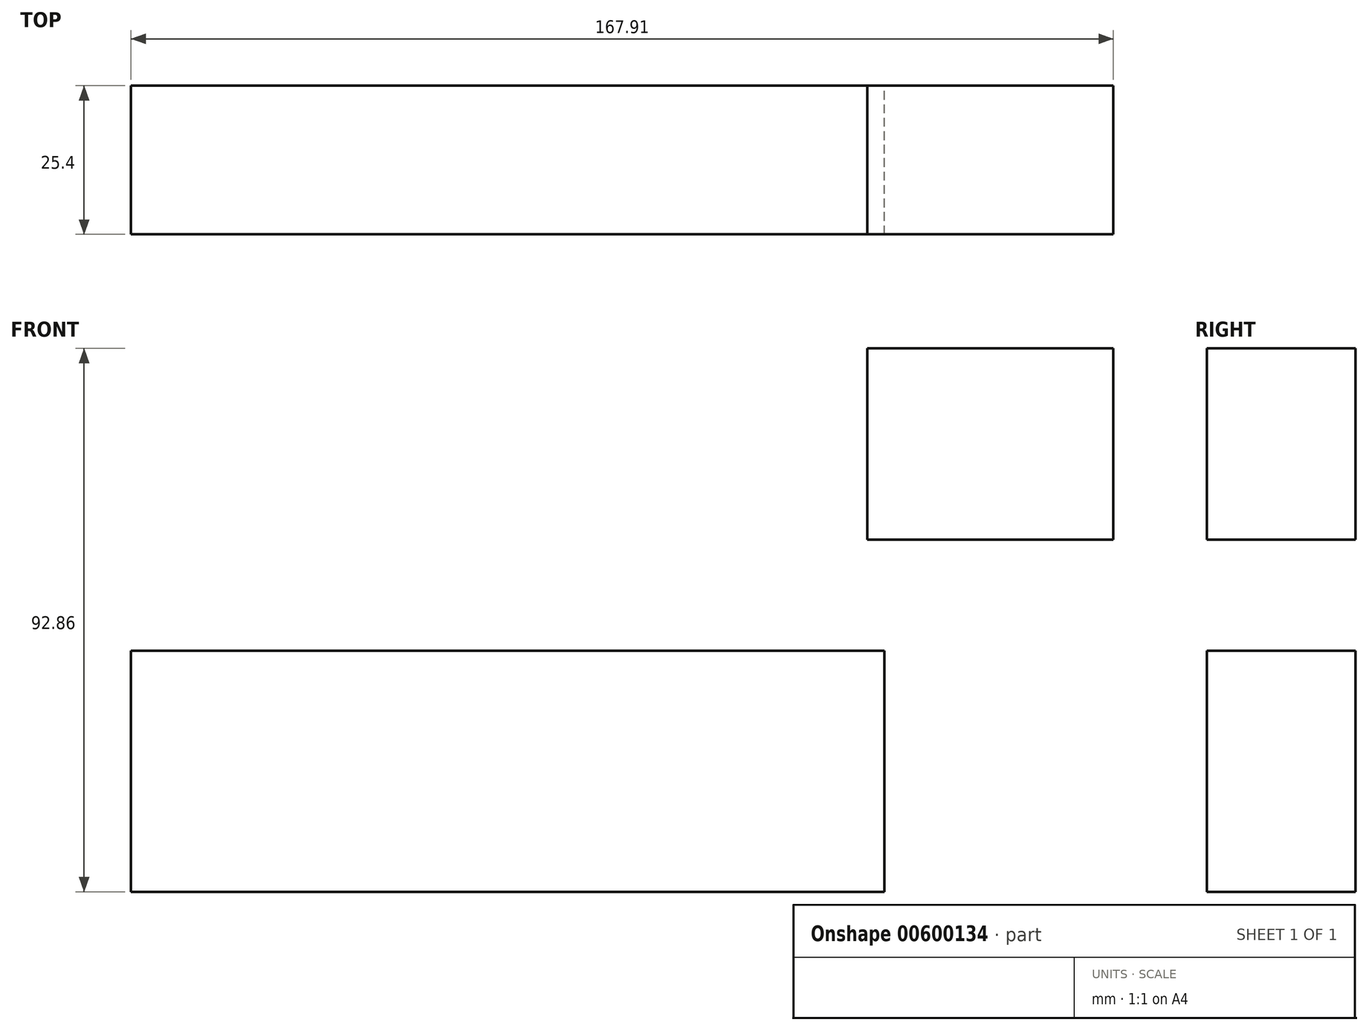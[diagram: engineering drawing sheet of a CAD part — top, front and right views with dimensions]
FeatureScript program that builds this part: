
annotation { "Feature Type Name" : "Feature", "Feature Type Description" : "" }
export const myFeature = defineFeature(function(context is Context, id is Id, definition is map)
    precondition{}
    {
        {
            var Q0;
            Q0=qCreatedBy(makeId("Front.planeOp"),FACE);
            var sketch = newSketch(context, id + "F0", { "sketchPlane" : qUnion([Q0])});
            skLineSegment(sketch, "E0.bottom", {"start": v(-64.39, -20.59) * mm, "end": v(64.39, -20.59) * mm});
            skLineSegment(sketch, "E0.top", {"start": v(-64.39, 20.59) * mm, "end": v(64.39, 20.59) * mm});
            skLineSegment(sketch, "E0.left", {"start": v(-64.39, -20.59) * mm, "end": v(-64.39, 20.59) * mm});
            skLineSegment(sketch, "E0.right", {"start": v(64.39, -20.59) * mm, "end": v(64.39, 20.59) * mm});
            skPoint(sketch, "E0.middle", {"position": v(0, 0) * mm});
            skLineSegment(sketch, "E1.bottom", {"start": v(103.52, 39.57) * mm, "end": v(61.47, 39.57) * mm});
            skLineSegment(sketch, "E1.top", {"start": v(103.52, 72.27) * mm, "end": v(61.47, 72.27) * mm});
            skLineSegment(sketch, "E1.left", {"start": v(103.52, 39.57) * mm, "end": v(103.52, 72.27) * mm});
            skLineSegment(sketch, "E1.right", {"start": v(61.47, 39.57) * mm, "end": v(61.47, 72.27) * mm});
            skPoint(sketch, "E1.middle", {"position": v(82.5, 55.92) * mm});
            skSolve(sketch);
        }
        {
            var Q0;
            Q0 = qSketchRegion(id + "F0", true);
            extrude(context, id + "F1", {"entities" : qUnion([Q0]), "depth" : 25.4 * mm, "offsetDistance" : 25.4 * mm});
        }
    });
